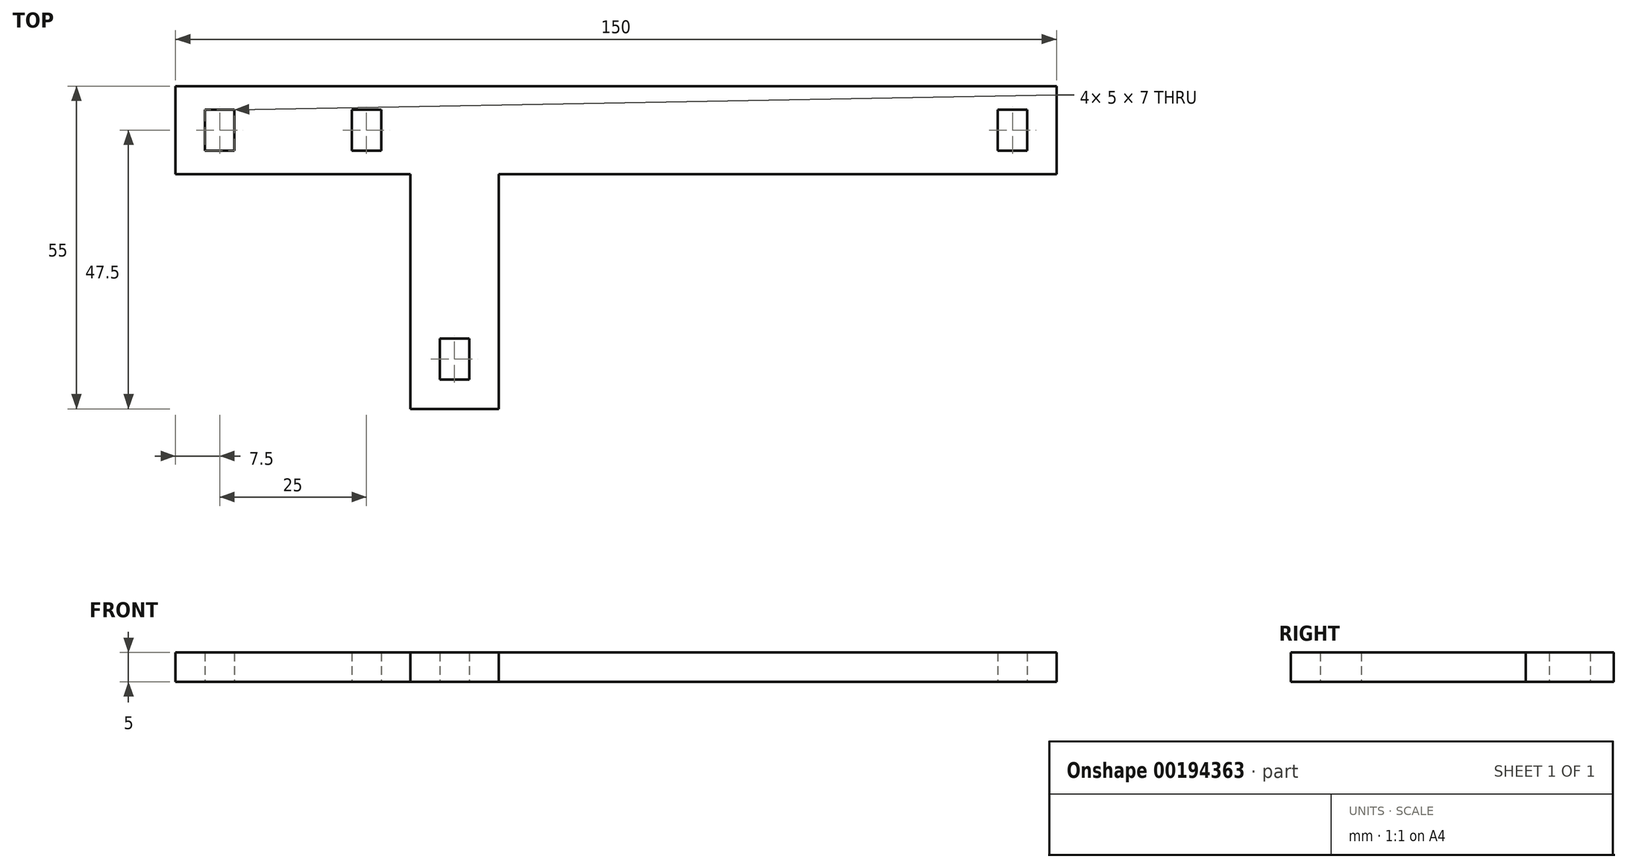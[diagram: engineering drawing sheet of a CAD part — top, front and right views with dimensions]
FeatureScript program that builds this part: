
annotation { "Feature Type Name" : "Feature", "Feature Type Description" : "" }
export const myFeature = defineFeature(function(context is Context, id is Id, definition is map)
    precondition{}
    {
        {
            var Q0;
            Q0=qCreatedBy(makeId("Top.planeOp"),FACE);
            var sketch = newSketch(context, id + "F0", { "sketchPlane" : qUnion([Q0])});
            skLineSegment(sketch, "E0", {"start": v(0, 0) * mm, "end": v(0, 15) * mm});
            skLineSegment(sketch, "E1", {"start": v(0, 15) * mm, "end": v(150, 15) * mm});
            skLineSegment(sketch, "E2", {"start": v(150, 15) * mm, "end": v(150, 0) * mm});
            skLineSegment(sketch, "E3", {"start": v(150, 0) * mm, "end": v(55, 0) * mm});
            skLineSegment(sketch, "E4", {"start": v(55, 0) * mm, "end": v(55, -40) * mm});
            skLineSegment(sketch, "E5", {"start": v(55, -40) * mm, "end": v(40, -40) * mm});
            skLineSegment(sketch, "E6", {"start": v(40, -40) * mm, "end": v(40, 0) * mm});
            skLineSegment(sketch, "E7", {"start": v(40, 0) * mm, "end": v(0, 0) * mm});
            skLineSegment(sketch, "E8", {"start": v(0, 7.5) * mm, "end": v(150, 7.5) * mm, "construction": true});
            skLineSegment(sketch, "E9", {"start": v(47.5, -40) * mm, "end": v(47.5, 7.5) * mm, "construction": true});
            skLineSegment(sketch, "E10.bottom", {"start": v(5, 11) * mm, "end": v(10, 11) * mm});
            skLineSegment(sketch, "E10.top", {"start": v(5, 4) * mm, "end": v(10, 4) * mm});
            skLineSegment(sketch, "E10.left", {"start": v(5, 11) * mm, "end": v(5, 4) * mm});
            skLineSegment(sketch, "E10.right", {"start": v(10, 11) * mm, "end": v(10, 4) * mm});
            skPoint(sketch, "E10.middle", {"position": v(7.5, 7.5) * mm});
            skLineSegment(sketch, "E11.bottom", {"start": v(30, 11) * mm, "end": v(35, 11) * mm});
            skLineSegment(sketch, "E11.top", {"start": v(30, 4) * mm, "end": v(35, 4) * mm});
            skLineSegment(sketch, "E11.left", {"start": v(30, 11) * mm, "end": v(30, 4) * mm});
            skLineSegment(sketch, "E11.right", {"start": v(35, 11) * mm, "end": v(35, 4) * mm});
            skPoint(sketch, "E11.middle", {"position": v(32.5, 7.5) * mm});
            skLineSegment(sketch, "E12.bottom", {"start": v(50, -28) * mm, "end": v(45, -28) * mm});
            skLineSegment(sketch, "E12.top", {"start": v(50, -35) * mm, "end": v(45, -35) * mm});
            skLineSegment(sketch, "E12.left", {"start": v(50, -28) * mm, "end": v(50, -35) * mm});
            skLineSegment(sketch, "E12.right", {"start": v(45, -28) * mm, "end": v(45, -35) * mm});
            skPoint(sketch, "E12.middle", {"position": v(47.5, -31.5) * mm});
            skLineSegment(sketch, "E13.bottom", {"start": v(140, 4) * mm, "end": v(145, 4) * mm});
            skLineSegment(sketch, "E13.top", {"start": v(140, 11) * mm, "end": v(145, 11) * mm});
            skLineSegment(sketch, "E13.left", {"start": v(140, 4) * mm, "end": v(140, 11) * mm});
            skLineSegment(sketch, "E13.right", {"start": v(145, 4) * mm, "end": v(145, 11) * mm});
            skPoint(sketch, "E13.middle", {"position": v(142.5, 7.5) * mm});
            skSolve(sketch);
        }
        {
            var Q0;
            Q0=makeQuery(id+"F0.imprint","IMPRINT",FACE,{"disambiguationData":[TD([[makeQuery(id+"F0.imprint","IMPRINT",EDGE,{"derivedFrom":sQuery(id+"F0.wireOp",EDGE,"E0")}),-1.0]])]});
            extrude(context, id + "F1", {"entities" : qUnion([Q0]), "depth" : 5 * mm});
        }
    });
